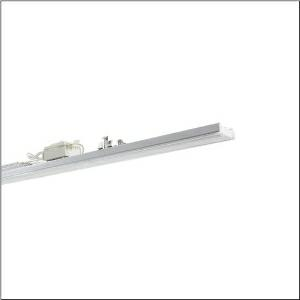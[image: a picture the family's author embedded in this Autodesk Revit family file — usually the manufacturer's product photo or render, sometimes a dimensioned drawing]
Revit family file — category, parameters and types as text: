
# Revit family: licross_21_recessed_mo_52tl12dn4axg3c
name_source: partatom
category: Lighting Fixtures
units: mm (PartAtom-declared; Revit-internal decimal feet)

## family parameters
Cut with Voids When Loaded = No
Host = Face
Light Source = No
Part Type = Normal
Room Calculation Point = No
Round Connector Dimension = Use Diameter
Shared = No

## types (1)
- --- (1 x LED, 950 lm, 6.7 W, 4000K)
    Apparent Load = 7 VA
    CIE Flux Codes = 72 92 99 100 100
    Color Rendering = 80
    Color Temperature = 4000K
    Default Elevation = 1800 mm
    Description = Licross 21 Recessed MO, luminaire insert, of sheet steel, galvanised, coil coated, white, length: 1.500mm, width: 66mm, height: 67mm, LED rated luminous flux: 10.280lm, light colour: 840, SDCM (Standard Deviation of Colour Matching)MacAdam ≤ 3 SDCM (initial), control gear: DALI 2 (for two DALI lines), with plug, 6-pole, with phase selection, for trunking rail, 14-core, mains connection: 220..240V, AC, 50/60Hz, rated input power: 62W, internal wiring halogen-free, for emergency light function, for trunking rail, 14-core, converter,control gear: single battery element, battery: LiFePO4, 9Ah, primary optical cover: cover, of PMMA, light emission: direct distribution, primary light characteristic: symmetric, protection rating (complete): IP40, insulation class (complete): insulation class I (protective earthing), certification: CE, UKCA, protection symbol: D if used in an environment without relevant dust loads with corresponding accessories, impact resistance: IK06, permissible ambient temperature for indoor applications: +5..+35°C, standard: EN 60598-2-22, LABS conformity tested according to VDMA 24364:2018-05, reducing of maximum allowable ambient temperature of 5°C with ceiling mounting, corresponds to IFS (International Featured Standards) requirements for safety and quality in the food industry, The light source and the operating device comply with the requirements of the Ecodesign Regulation (EU) 2019/2020 and are replaceable in accordance with this regulation, packaging unit: 1 piece
    Height = 58 mm
    Lamp = 1 x LED
    Lamp Light Flux = 950 lm
    Lamp Power = 6.7 W
    Lamp count = 1
    Length = 1500 mm
    Luminous efficacy = 142 lm/W
    Manufacturer = Siteco
    ModVariant = No
    Model = 52TL12DN4AXG3C
    Mounting Place = Ceiling
    Mounting Type = Pendant
    Number of Poles = 1
    OnlyDefault = Yes
    Power Factor = 1
    Product Name = Licross 21 Recessed MO
    Product group = luminaire insert | ceiling pendant
    ProductGroupID = 901
    Protection Class = Protection class I
    Protection Degree = IP 40
    RLX_Detail_Level = 1
    RLX_Emergency_Light_Flux = 0 lm
    RLX_Emergency_Type = 0
    RLX_Emergency_Type_DB = No
    RlxData = <blob elided: 25325 chars, md5=353a6d07>
    Socket = socket
    Standby Power = 0 W
    System Light Flux = 950 lm
    System Power = 7 W
    Type Comments = : emergency light operation: 3 h
    Type Image = l_1296930.jpg
    URL = http://relux.com
    VarID = @adj_110003
    Voltage = 0 V
    Weight = 0.00 kg
    Width = 66 mm

## geometry (parser evidence)
native form markers: Blend x4, Sweep x13
no freeform markers — native parametric forms only
